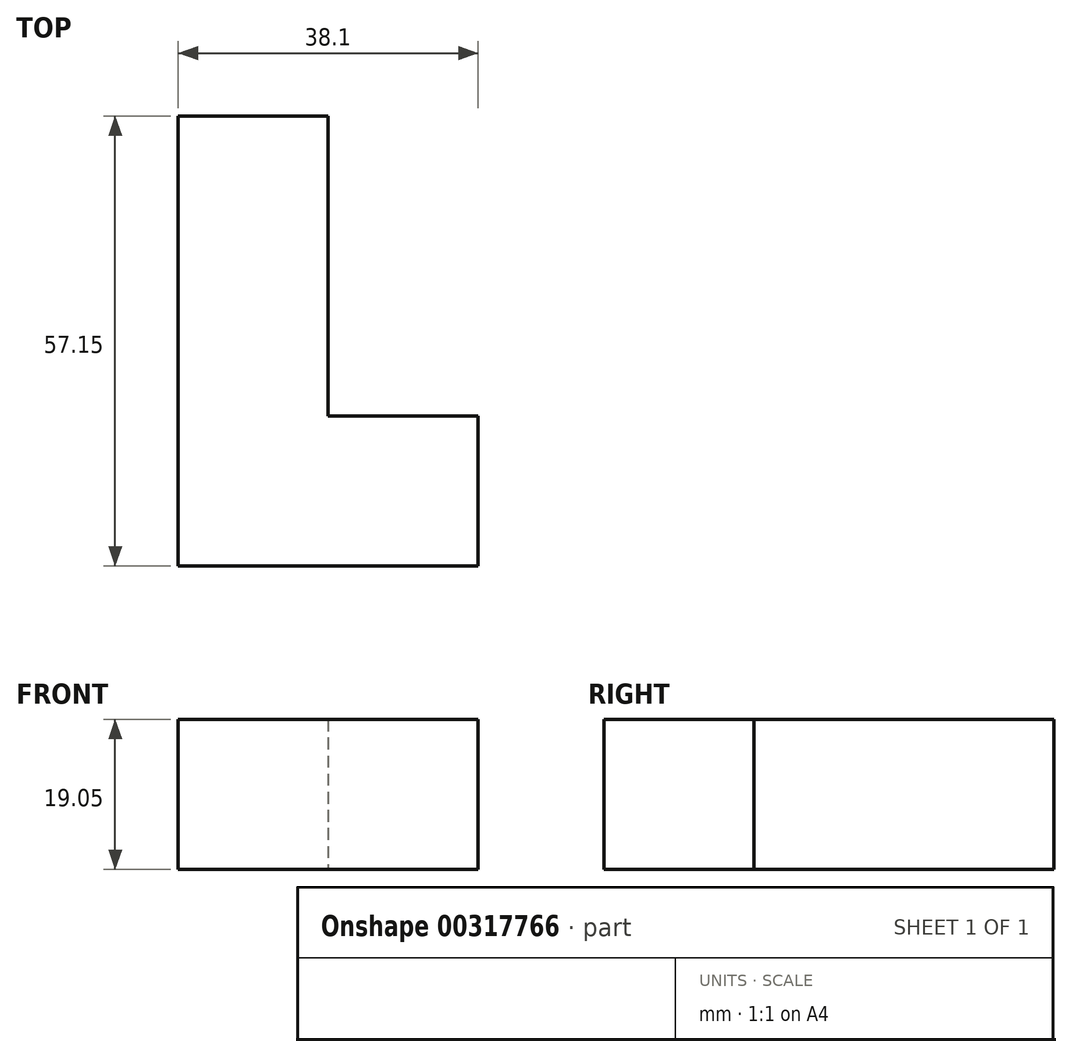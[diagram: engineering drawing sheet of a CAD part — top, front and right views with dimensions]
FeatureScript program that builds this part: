
annotation { "Feature Type Name" : "Feature", "Feature Type Description" : "" }
export const myFeature = defineFeature(function(context is Context, id is Id, definition is map)
    precondition{}
    {
        {
            var Q0;
            Q0=qCreatedBy(makeId("Top.planeOp"),FACE);
            var sketch = newSketch(context, id + "F0", { "sketchPlane" : qUnion([Q0])});
            skLineSegment(sketch, "E0.bottom", {"start": v(0, 0) * mm, "end": v(19.05, 0) * mm});
            skLineSegment(sketch, "E0.top", {"start": v(0, 57.15) * mm, "end": v(19.05, 57.15) * mm});
            skLineSegment(sketch, "E0.left", {"start": v(0, 0) * mm, "end": v(0, 57.15) * mm});
            skLineSegment(sketch, "E0.right", {"start": v(19.05, 19.05) * mm, "end": v(19.05, 57.15) * mm});
            skLineSegment(sketch, "E1.left", {"start": v(0, 0) * mm, "end": v(0, 19.05) * mm});
            skLineSegment(sketch, "E2", {"start": v(19.05, 19.05) * mm, "end": v(38.1, 19.05) * mm});
            skLineSegment(sketch, "E3", {"start": v(38.1, 19.05) * mm, "end": v(38.1, 0) * mm});
            skLineSegment(sketch, "E4", {"start": v(38.1, 0) * mm, "end": v(19.05, 0) * mm});
            skSolve(sketch);
        }
        {
            var Q0;
            Q0 = qSketchRegion(id + "F0", true);
            extrude(context, id + "F1", {"entities" : qUnion([Q0]), "depth" : 19.05 * mm});
        }
    });
